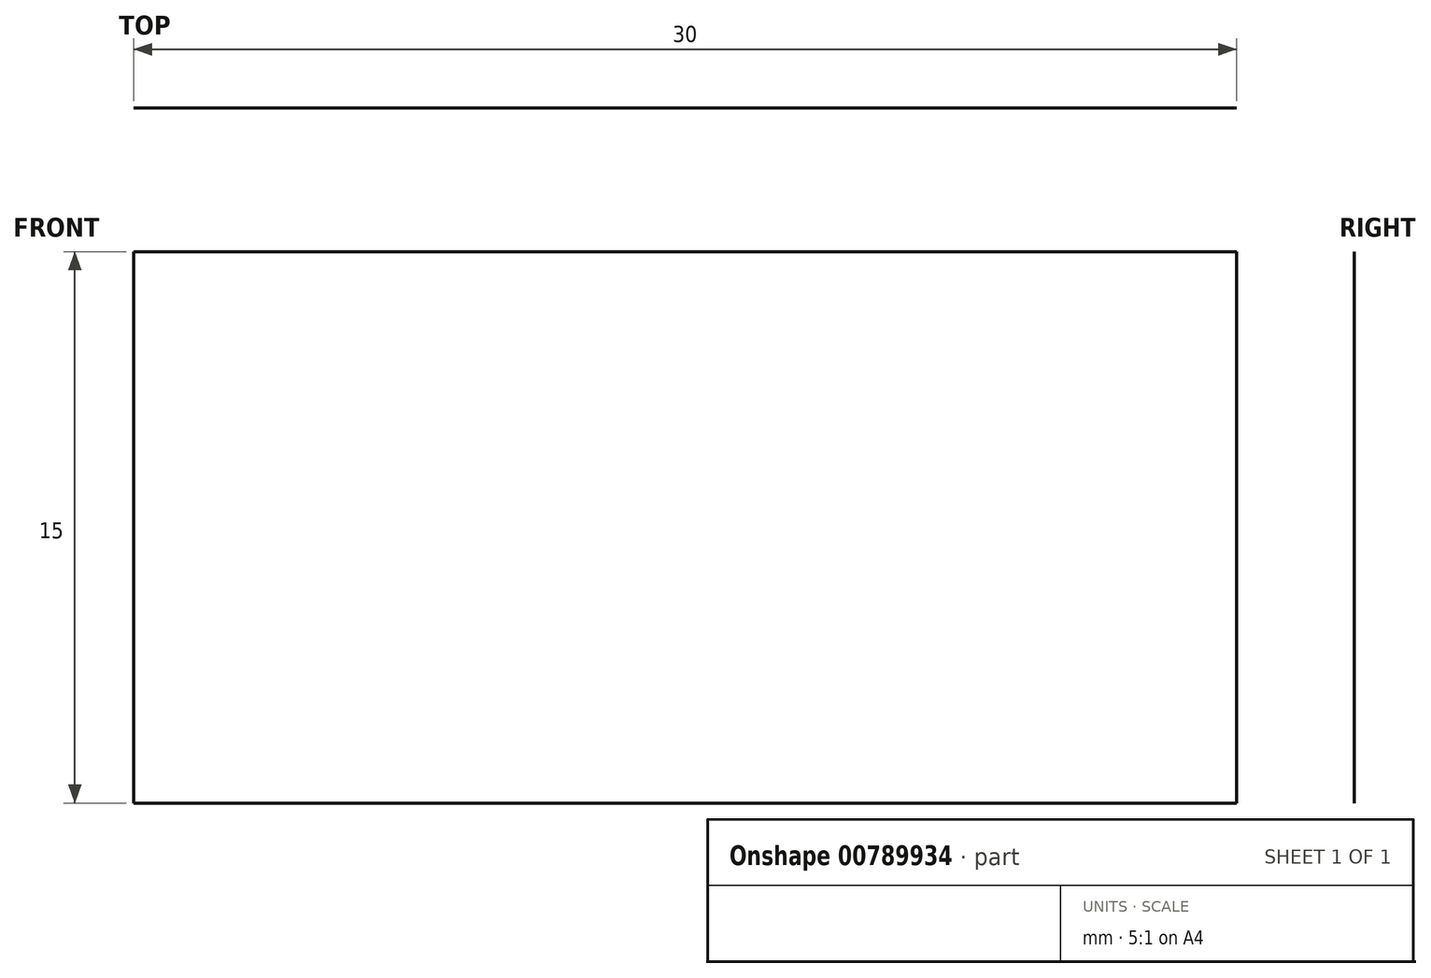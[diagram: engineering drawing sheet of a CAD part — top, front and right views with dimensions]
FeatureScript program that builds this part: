
annotation { "Feature Type Name" : "Feature", "Feature Type Description" : "" }
export const myFeature = defineFeature(function(context is Context, id is Id, definition is map)
    precondition{}
    {
        {
            var Q0;
            Q0=qCreatedBy(makeId("Right.planeOp"),FACE);
            var sketch = newSketch(context, id + "F0", { "sketchPlane" : qUnion([Q0])});
            skLineSegment(sketch, "E0", {"start": v(0, 0) * mm, "end": v(15, 0) * mm});
            skLineSegment(sketch, "E1", {"start": v(0, 0) * mm, "end": v(0, 15) * mm});
            skSolve(sketch);
        }
        {
            var Q0;
            Q0=sQuery(id+"F0.wireOp",EDGE,"E1");
            extrude(context, id + "F1", {"bodyType" : ToolBodyType.SURFACE, "surfaceEntities" : qUnion([Q0]), "depth" : 30 * mm, "offsetDistance" : 25 * mm});
        }
    });
